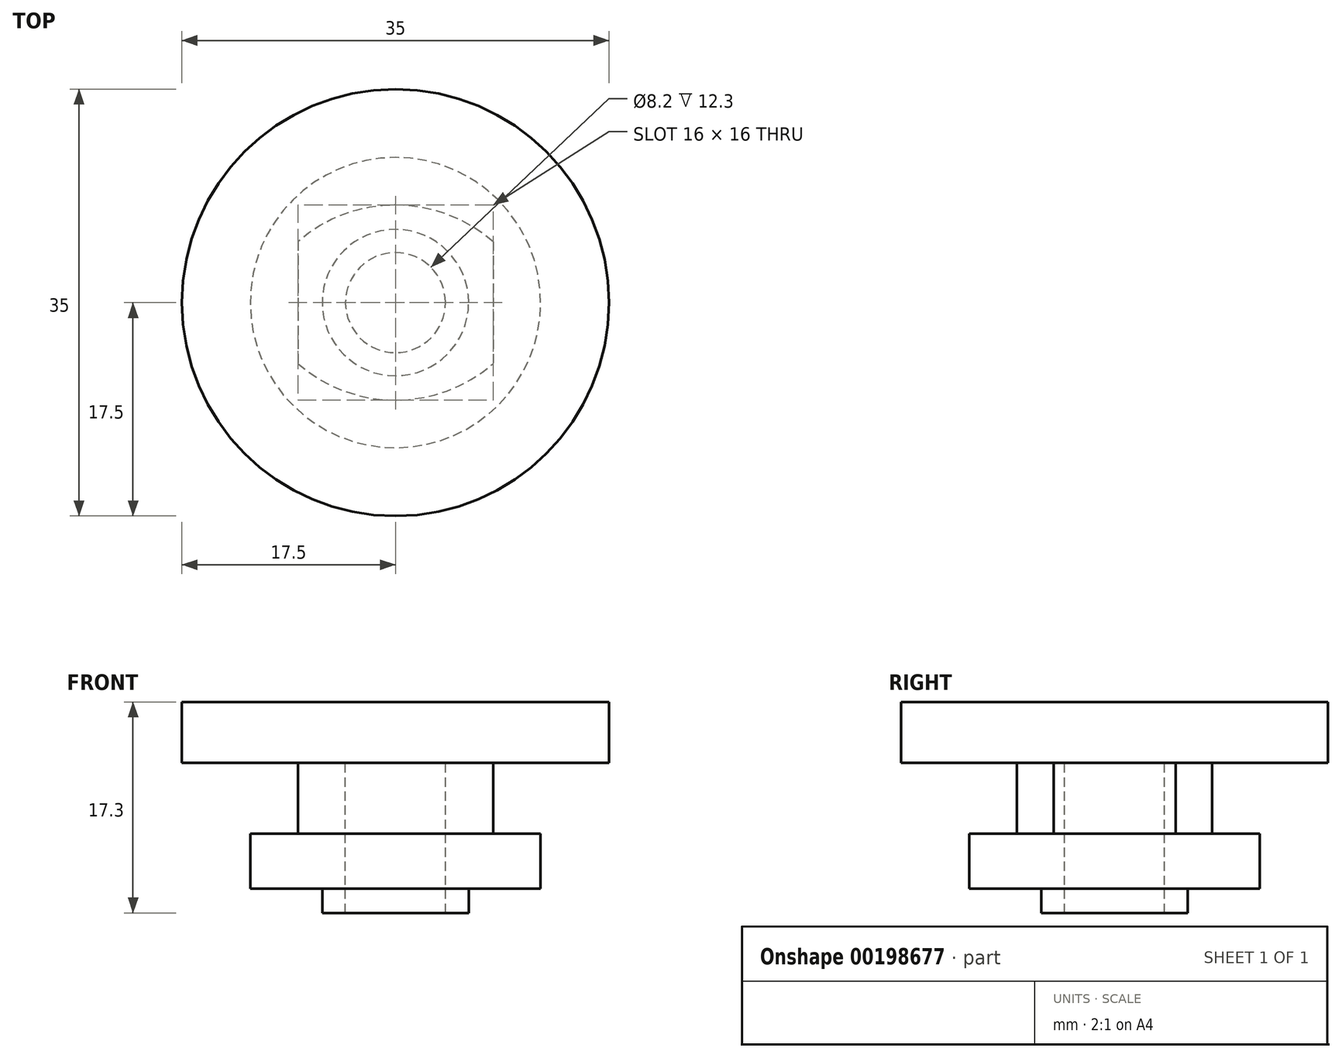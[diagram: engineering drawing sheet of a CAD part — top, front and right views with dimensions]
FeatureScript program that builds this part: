
annotation { "Feature Type Name" : "Feature", "Feature Type Description" : "" }
export const myFeature = defineFeature(function(context is Context, id is Id, definition is map)
    precondition{}
    {
        {
            var Q0;
            Q0=qCreatedBy(makeId("Front.planeOp"),FACE);
            var sketch = newSketch(context, id + "F0", { "sketchPlane" : qUnion([Q0])});
            skLineSegment(sketch, "E0.bottom", {"start": v(0, 17.3) * mm, "end": v(17.5, 17.3) * mm});
            skLineSegment(sketch, "E0.top", {"start": v(0, 12.3) * mm, "end": v(17.5, 12.3) * mm});
            skLineSegment(sketch, "E0.left", {"start": v(0, 17.3) * mm, "end": v(0, 12.3) * mm});
            skLineSegment(sketch, "E0.right", {"start": v(17.5, 17.3) * mm, "end": v(17.5, 12.3) * mm});
            skLineSegment(sketch, "E1.bottom", {"start": v(8, 12.3) * mm, "end": v(4.1, 12.3) * mm});
            skLineSegment(sketch, "E1.top", {"start": v(8, 6.5) * mm, "end": v(4.1, 6.5) * mm});
            skLineSegment(sketch, "E1.left", {"start": v(8, 12.3) * mm, "end": v(8, 6.5) * mm});
            skLineSegment(sketch, "E1.right", {"start": v(4.1, 12.3) * mm, "end": v(4.1, 6.5) * mm});
            skLineSegment(sketch, "E2.bottom", {"start": v(4.1, 6.5) * mm, "end": v(11.9, 6.5) * mm});
            skLineSegment(sketch, "E2.top", {"start": v(4.1, 2) * mm, "end": v(11.9, 2) * mm});
            skLineSegment(sketch, "E2.left", {"start": v(4.1, 6.5) * mm, "end": v(4.1, 2) * mm});
            skLineSegment(sketch, "E2.right", {"start": v(11.9, 6.5) * mm, "end": v(11.9, 2) * mm});
            skLineSegment(sketch, "E3.bottom", {"start": v(4.1, 2) * mm, "end": v(6, 2) * mm});
            skLineSegment(sketch, "E3.top", {"start": v(4.1, 0) * mm, "end": v(6, 0) * mm});
            skLineSegment(sketch, "E3.left", {"start": v(4.1, 2) * mm, "end": v(4.1, 0) * mm});
            skLineSegment(sketch, "E3.right", {"start": v(6, 2) * mm, "end": v(6, 0) * mm});
            skSolve(sketch);
        }
        {
            var Q0;
            Q0 = qSketchRegion(id + "F0", true);
            var Q1;
            Q1=sQuery(id+"F0.wireOp",EDGE,"E0.left");
            revolve(context, id + "F1", {"entities" : qUnion([Q0]), "axis" : qUnion([Q1]), "revolveType" : RevolveType.FULL});
        }
        {
            var Q0;
            {var subQ0=sQuery(id+"F0.wireOp",EDGE,"E0.top");Q0=makeQuery(id+"F1.opRevolve","SWEPT_FACE",FACE,{"disambiguationData":[OSD([subQ0]),TDD([makeQuery(id+"F0.imprint","IMPRINT",EDGE,{"disambiguationData":[TD([[makeQuery(id+"F0.imprint","INTERSECT",VERTEX,{"derivedFrom":[subQ0,sQuery(id+"F0.wireOp",EDGE,"E0.right")]}),1.0]])],"derivedFrom":subQ0})])]});}
            var sketch = newSketch(context, id + "F2", { "sketchPlane" : qUnion([Q0])});
            skLineSegment(sketch, "E4.left", {"start": v(8, -5) * mm, "end": v(8, 5) * mm});
            skLineSegment(sketch, "E4.right", {"start": v(-8, -5) * mm, "end": v(-8, 5) * mm});
            skLineSegment(sketch, "E5.left", {"start": v(8, 5) * mm, "end": v(8, -5) * mm});
            skLineSegment(sketch, "E5.right", {"start": v(-8, 5) * mm, "end": v(-8, -5) * mm});
            skArc(sketch, "E6", {"start": v(-8, -5) * mm, "mid": v(0, -8) * mm, "end": v(8, -5) * mm});
            skArc(sketch, "E7", {"start": v(8, 5) * mm, "mid": v(0, 8) * mm, "end": v(-8, 5) * mm});
            skPoint(sketch, "E8.orphan", {"position": v(0, -8) * mm});
            skPoint(sketch, "E9.orphan", {"position": v(0, 8) * mm});
            skCircle(sketch, "E10", {"center": v(0, 0) * mm, "radius": 4.17 * mm});
            skSolve(sketch);
        }
        {
            var Q0;
            Q0 = qSketchRegion(id + "F2", true);
            extrude(context, id + "F3", {"entities" : qUnion([Q0]), "operationType" : NewBodyOperationType.ADD, "depth" : 6 * mm});
        }
    });
